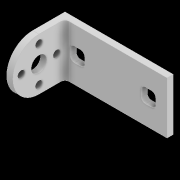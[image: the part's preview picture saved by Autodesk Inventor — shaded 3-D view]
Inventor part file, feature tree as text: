
AUTODESK INVENTOR PART (.ipt)
format: ipt  version: 2020 (Build 240168000, 168)  size: 166,912 bytes
history: native  units: mm
features: sketch x5, extrude x3, hole x2, fillet x1, pattern_circular x1
ambient origin geometry x8: Origin, YZ Plane, XZ Plane, XY Plane, X Axis, Y Axis, Z Axis, Center Point
bodies: Solid1 (feature_tree)
feature tree (12):
  extrude  "Extrusion1"  Depth=25.0mm
  extrude  "Extrusion2"  Depth=7.0mm
  extrude  "Extrusion3"  Depth=5.458315mm
  fillet  "Fillet1"  Radius=3.0mm
  hole  "Hole1"  [1 undecoded]
  hole  "Hole2"  [1 undecoded]
  pattern_circular  "Circular Pattern1"  [2 undecoded]
  sketch  "Sketch1"  dims[d0=52.0mm d1=25.0mm]
  sketch  "Sketch2"  dims[d2=7.0mm d3=7.0mm]
  sketch  "Sketch3"  dims[d4=2.0mm d5=5.458315mm]
  sketch  "Sketch4"  dims[d6=7.0mm d7=7.0mm d8=2.0mm d9=5.458315mm d10=3.0mm d11=0.0mm]
  sketch  "Sketch5"  dims[d12=3.0mm d13=25.0mm d14=0.0mm d16=12.5mm d17=25.0mm d18=0.0mm d19=2.0mm d20=7.5mm d21=6.0mm d22=4.0mm d23=2.0mm d24=90.0deg d25=8.0mm d26=0.0mm d27=15.5mm d28=8.5mm d29=3.4mm d30=6.0mm d31=4.0mm d32=2.0mm d33=90.0deg d34=8.0mm d35=0.0mm d36=40.0mm d37=360.0deg]
note: 4 required parameter values undecoded (feature->parameter linkage not recoverable at this tier; creation-order binding heuristic only, values carry confidence <= 0.55)
